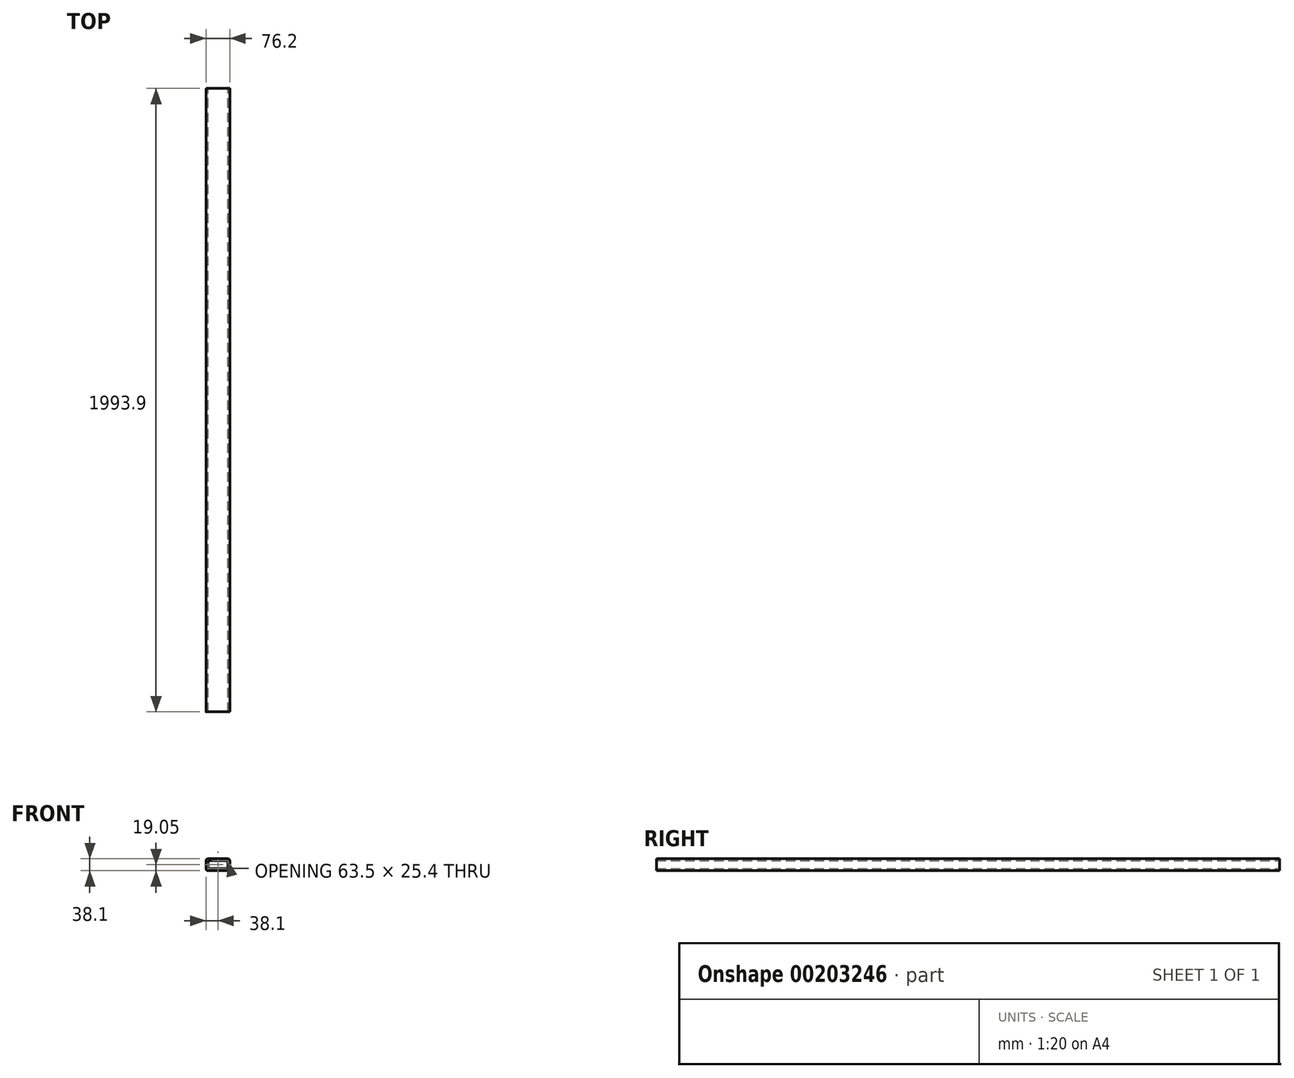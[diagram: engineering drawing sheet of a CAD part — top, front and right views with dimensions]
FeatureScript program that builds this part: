
annotation { "Feature Type Name" : "Feature", "Feature Type Description" : "" }
export const myFeature = defineFeature(function(context is Context, id is Id, definition is map)
    precondition{}
    {
        {
            var Q0;
            Q0=qCreatedBy(makeId("Front.planeOp"),FACE);
            var sketch = newSketch(context, id + "F0", { "sketchPlane" : qUnion([Q0])});
            skLineSegment(sketch, "E0.bottom", {"start": v(6.35, 0) * mm, "end": v(69.85, 0) * mm});
            skLineSegment(sketch, "E0.top", {"start": v(6.35, 38.1) * mm, "end": v(69.85, 38.1) * mm});
            skLineSegment(sketch, "E0.left", {"start": v(0, 6.35) * mm, "end": v(0, 31.75) * mm});
            skLineSegment(sketch, "E0.right", {"start": v(76.2, 6.35) * mm, "end": v(76.2, 31.75) * mm});
            skLineSegment(sketch, "E1.bottom", {"start": v(12.7, 6.35) * mm, "end": v(63.5, 6.35) * mm});
            skLineSegment(sketch, "E1.top", {"start": v(12.7, 31.75) * mm, "end": v(63.5, 31.75) * mm});
            skLineSegment(sketch, "E1.left", {"start": v(6.35, 12.7) * mm, "end": v(6.35, 25.4) * mm});
            skLineSegment(sketch, "E1.right", {"start": v(69.85, 12.7) * mm, "end": v(69.85, 25.4) * mm});
            skPoint(sketch, "E2.visualSharp", {"position": v(76.2, 38.1) * mm});
            skArc(sketch, "E2.filletArc", {"start": v(76.2, 31.75) * mm, "mid": v(74.34, 36.24) * mm, "end": v(69.85, 38.1) * mm});
            skPoint(sketch, "E3.visualSharp", {"position": v(76.2, 0) * mm});
            skArc(sketch, "E3.filletArc", {"start": v(69.85, 0) * mm, "mid": v(74.34, 1.86) * mm, "end": v(76.2, 6.35) * mm});
            skPoint(sketch, "E4.visualSharp", {"position": v(0, 0) * mm});
            skArc(sketch, "E4.filletArc", {"start": v(0, 6.35) * mm, "mid": v(1.86, 1.86) * mm, "end": v(6.35, 0) * mm});
            skPoint(sketch, "E5.visualSharp", {"position": v(0, 38.1) * mm});
            skArc(sketch, "E5.filletArc", {"start": v(6.35, 38.1) * mm, "mid": v(1.86, 36.24) * mm, "end": v(0, 31.75) * mm});
            skArc(sketch, "E6.filletArc", {"start": v(12.7, 31.75) * mm, "mid": v(8.2, 29.9) * mm, "end": v(6.35, 25.4) * mm});
            skArc(sketch, "E7.filletArc", {"start": v(69.85, 25.4) * mm, "mid": v(68, 29.9) * mm, "end": v(63.5, 31.75) * mm});
            skArc(sketch, "E8.filletArc", {"start": v(63.5, 6.35) * mm, "mid": v(68, 8.2) * mm, "end": v(69.85, 12.7) * mm});
            skArc(sketch, "E9.filletArc", {"start": v(6.35, 12.7) * mm, "mid": v(8.2, 8.2) * mm, "end": v(12.7, 6.35) * mm});
            skSolve(sketch);
        }
        {
            var Q0;
            Q0 = qSketchRegion(id + "F0", true);
            extrude(context, id + "F1", {"entities" : qUnion([Q0]), "depth" : 1993.9 * mm});
        }
    });
